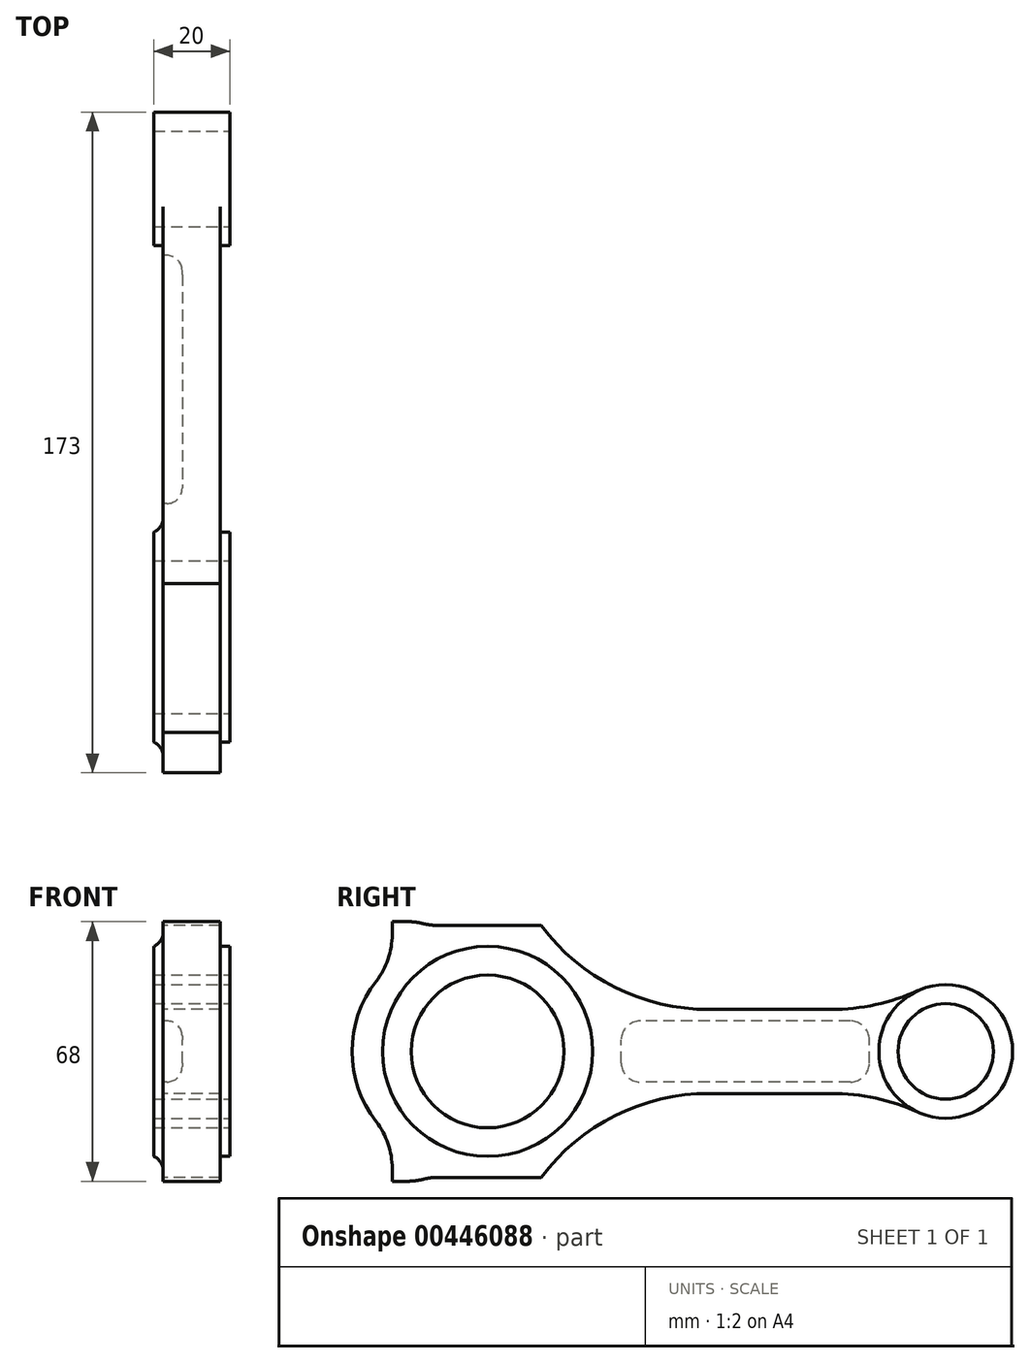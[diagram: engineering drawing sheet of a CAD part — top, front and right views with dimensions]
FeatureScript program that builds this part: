
annotation { "Feature Type Name" : "Feature", "Feature Type Description" : "" }
export const myFeature = defineFeature(function(context is Context, id is Id, definition is map)
    precondition{}
    {
        {
            var Q0;
            Q0=qCreatedBy(makeId("Right.planeOp"),FACE);
            var sketch = newSketch(context, id + "F0", { "sketchPlane" : qUnion([Q0])});
            skCircle(sketch, "E0", {"center": v(0, 0) * mm, "radius": 20 * mm});
            skCircle(sketch, "E1", {"center": v(0, 0) * mm, "radius": 27.5 * mm});
            skLineSegment(sketch, "E2", {"start": v(0, 0) * mm, "end": v(227.09, 0) * mm, "construction": true});
            skCircle(sketch, "E3", {"center": v(120, 0) * mm, "radius": 12.5 * mm});
            skCircle(sketch, "E4", {"center": v(120, 0) * mm, "radius": 17.5 * mm});
            skLineSegment(sketch, "E5", {"start": v(90, -11) * mm, "end": v(58, -11) * mm});
            skArc(sketch, "E6", {"start": v(58, -11) * mm, "mid": v(33.4, -16.8) * mm, "end": v(14, -33) * mm});
            skLineSegment(sketch, "E7", {"start": v(-13, -33) * mm, "end": v(14, -33) * mm});
            skArc(sketch, "E8", {"start": v(-13, -33) * mm, "mid": v(-15.02, -33.13) * mm, "end": v(-17, -33.5) * mm});
            skArc(sketch, "E9", {"start": v(-21, -34) * mm, "mid": v(-18.98, -33.87) * mm, "end": v(-17, -33.5) * mm});
            skLineSegment(sketch, "E10", {"start": v(-21, -34) * mm, "end": v(-25, -34) * mm});
            skLineSegment(sketch, "E11", {"start": v(-25, -34) * mm, "end": v(-25, -30.66) * mm});
            skArc(sketch, "E12", {"start": v(-25, -30.66) * mm, "mid": v(-26.08, -24.17) * mm, "end": v(-29.2, -18.4) * mm});
            skArc(sketch, "E13", {"start": v(-35.5, 0) * mm, "mid": v(-33.88, -9.72) * mm, "end": v(-29.2, -18.4) * mm});
            skArc(sketch, "E14", {"start": v(112.76, -15.93) * mm, "mid": v(101.64, -12.25) * mm, "end": v(90, -11) * mm});
            skArc(sketch, "E15.MirrorCS", {"start": v(-35.5, 0) * mm, "mid": v(-33.88, 9.72) * mm, "end": v(-29.2, 18.4) * mm});
            skArc(sketch, "E16.MirrorCS", {"start": v(-25, 30.66) * mm, "mid": v(-26.08, 24.17) * mm, "end": v(-29.2, 18.4) * mm});
            skLineSegment(sketch, "E17.MirrorCS", {"start": v(-25, 34) * mm, "end": v(-25, 30.66) * mm});
            skLineSegment(sketch, "E18.MirrorCS", {"start": v(-21, 34) * mm, "end": v(-25, 34) * mm});
            skArc(sketch, "E19.MirrorCS", {"start": v(-21, 34) * mm, "mid": v(-18.98, 33.87) * mm, "end": v(-17, 33.5) * mm});
            skArc(sketch, "E20.MirrorCS", {"start": v(-13, 33) * mm, "mid": v(-15.02, 33.13) * mm, "end": v(-17, 33.5) * mm});
            skLineSegment(sketch, "E21.MirrorCS", {"start": v(-13, 33) * mm, "end": v(14, 33) * mm});
            skArc(sketch, "E22.MirrorCS", {"start": v(58, 11) * mm, "mid": v(33.4, 16.8) * mm, "end": v(14, 33) * mm});
            skLineSegment(sketch, "E23.MirrorCS", {"start": v(90, 11) * mm, "end": v(58, 11) * mm});
            skArc(sketch, "E24.MirrorCS", {"start": v(112.76, 15.93) * mm, "mid": v(101.64, 12.25) * mm, "end": v(90, 11) * mm});
            skSolve(sketch);
        }
        {
            var Q0;
            Q0=makeQuery(id+"F0.imprint","IMPRINT",FACE,{"disambiguationData":[TD([[makeQuery(id+"F0.imprint","IMPRINT",EDGE,{"derivedFrom":sQuery(id+"F0.wireOp",EDGE,"E0")}),-1.0]])]});
            var Q1;
            Q1=makeQuery(id+"F0.imprint","IMPRINT",FACE,{"disambiguationData":[TD([[makeQuery(id+"F0.imprint","IMPRINT",EDGE,{"derivedFrom":sQuery(id+"F0.wireOp",EDGE,"E3")}),-1.0]])]});
            extrude(context, id + "F1", {"entities" : qUnion([Q0, Q1]), "endBound" : BoundingType.SYMMETRIC, "oppositeDirection" : true, "depth" : 20 * mm, "offsetDistance" : 25 * mm});
        }
        {
            var Q0;
            Q0=makeQuery(id+"F0.imprint","IMPRINT",FACE,{"disambiguationData":[TD([[makeQuery(id+"F0.imprint","IMPRINT",EDGE,{"derivedFrom":sQuery(id+"F0.wireOp",EDGE,"E1")}),-1.0]])]});
            extrude(context, id + "F2", {"entities" : qUnion([Q0]), "operationType" : NewBodyOperationType.ADD, "endBound" : BoundingType.SYMMETRIC, "depth" : 15 * mm, "offsetDistance" : 25 * mm});
        }
        {
            var Q0;
            Q0=makeQuery(id+"F2.opExtrude","CAP_FACE",FACE,{"disambiguationData":[OSD([sQuery(id+"F0.wireOp",EDGE,"E1"),sQuery(id+"F0.wireOp",EDGE,"E4"),sQuery(id+"F0.wireOp",EDGE,"E5"),sQuery(id+"F0.wireOp",EDGE,"E6"),sQuery(id+"F0.wireOp",EDGE,"E7"),sQuery(id+"F0.wireOp",EDGE,"E8"),sQuery(id+"F0.wireOp",EDGE,"E9"),sQuery(id+"F0.wireOp",EDGE,"E10"),sQuery(id+"F0.wireOp",EDGE,"E11"),sQuery(id+"F0.wireOp",EDGE,"E12"),sQuery(id+"F0.wireOp",EDGE,"E13"),sQuery(id+"F0.wireOp",EDGE,"E14"),sQuery(id+"F0.wireOp",EDGE,"E15.MirrorCS"),sQuery(id+"F0.wireOp",EDGE,"E16.MirrorCS"),sQuery(id+"F0.wireOp",EDGE,"E17.MirrorCS"),sQuery(id+"F0.wireOp",EDGE,"E18.MirrorCS"),sQuery(id+"F0.wireOp",EDGE,"E19.MirrorCS"),sQuery(id+"F0.wireOp",EDGE,"E20.MirrorCS"),sQuery(id+"F0.wireOp",EDGE,"E21.MirrorCS"),sQuery(id+"F0.wireOp",EDGE,"E22.MirrorCS"),sQuery(id+"F0.wireOp",EDGE,"E23.MirrorCS"),sQuery(id+"F0.wireOp",EDGE,"E24.MirrorCS")])],"isStart":true});
            var sketch = newSketch(context, id + "F3", { "sketchPlane" : qUnion([Q0])});
            skLineSegment(sketch, "E25.bottom", {"start": v(-100, -8) * mm, "end": v(-35, -8) * mm});
            skLineSegment(sketch, "E25.top", {"start": v(-100, 8) * mm, "end": v(-35, 8) * mm});
            skLineSegment(sketch, "E25.left", {"start": v(-100, -8) * mm, "end": v(-100, 8) * mm});
            skLineSegment(sketch, "E25.right", {"start": v(-35, -8) * mm, "end": v(-35, 8) * mm});
            skSolve(sketch);
        }
        {
            var Q0;
            Q0=makeQuery(id+"F3.imprint","IMPRINT",FACE,{"disambiguationData":[TD([[makeQuery(id+"F3.imprint","IMPRINT",EDGE,{"derivedFrom":sQuery(id+"F3.wireOp",EDGE,"E25.bottom")}),1.0]])]});
            extrude(context, id + "F4", {"entities" : qUnion([Q0]), "operationType" : NewBodyOperationType.REMOVE, "oppositeDirection" : true, "depth" : 5 * mm, "offsetDistance" : 25 * mm});
        }
        {
            var Q0;
            Q0=makeQuery(id+"F4.boolean.opBoolean","COPY",EDGE,{"derivedFrom":makeQuery(id+"F4.opExtrude","SWEPT_EDGE",EDGE,{"disambiguationData":[OSD([sQuery(id+"F3.wireOp",EDGE,"E25.top"),sQuery(id+"F3.wireOp",EDGE,"E25.left")])]})});
            var Q1;
            Q1=makeQuery(id+"F4.boolean.opBoolean","COPY",EDGE,{"derivedFrom":makeQuery(id+"F4.opExtrude","SWEPT_EDGE",EDGE,{"disambiguationData":[OSD([sQuery(id+"F3.wireOp",EDGE,"E25.bottom"),sQuery(id+"F3.wireOp",EDGE,"E25.left")])]})});
            var Q2;
            Q2=makeQuery(id+"F4.boolean.opBoolean","COPY",EDGE,{"derivedFrom":makeQuery(id+"F4.opExtrude","SWEPT_EDGE",EDGE,{"disambiguationData":[OSD([sQuery(id+"F3.wireOp",EDGE,"E25.bottom"),sQuery(id+"F3.wireOp",EDGE,"E25.right")])]})});
            var Q3;
            Q3=makeQuery(id+"F4.boolean.opBoolean","COPY",EDGE,{"derivedFrom":makeQuery(id+"F4.opExtrude","SWEPT_EDGE",EDGE,{"disambiguationData":[OSD([sQuery(id+"F3.wireOp",EDGE,"E25.top"),sQuery(id+"F3.wireOp",EDGE,"E25.right")])]})});
            fillet(context, id + "F5", {"entities" : qUnion([Q0, Q1, Q2, Q3]), "radius" : 5 * mm, "allowEdgeOverflow" : false});
        }
        {
            var Q0;
            Q0=makeQuery(id+"F4.boolean.opBoolean","COPY",FACE,{"derivedFrom":makeQuery(id+"F4.opExtrude","CAP_FACE",FACE,{"disambiguationData":[OSD([sQuery(id+"F3.wireOp",EDGE,"E25.bottom"),sQuery(id+"F3.wireOp",EDGE,"E25.top"),sQuery(id+"F3.wireOp",EDGE,"E25.left"),sQuery(id+"F3.wireOp",EDGE,"E25.right")])],"isStart":false})});
            fillet(context, id + "F6", {"entities" : qUnion([Q0]), "radius" : 4 * mm, "tangentPropagation" : true, "allowEdgeOverflow" : false});
        }
        {
            var Q0;
            Q0=makeQuery(id+"F2.opExtrude","CAP_EDGE",EDGE,{"disambiguationData":[OSD([sQuery(id+"F0.wireOp",EDGE,"E1")])],"isStart":true});
            var Q1;
            Q1=makeQuery(id+"F2.opExtrude","CAP_EDGE",EDGE,{"disambiguationData":[OSD([sQuery(id+"F0.wireOp",EDGE,"E1")])],"isStart":false});
            fillet(context, id + "F7", {"entities" : qUnion([Q0, Q1]), "radius" : 4 * mm, "tangentPropagation" : true, "allowEdgeOverflow" : false});
        }
    });
